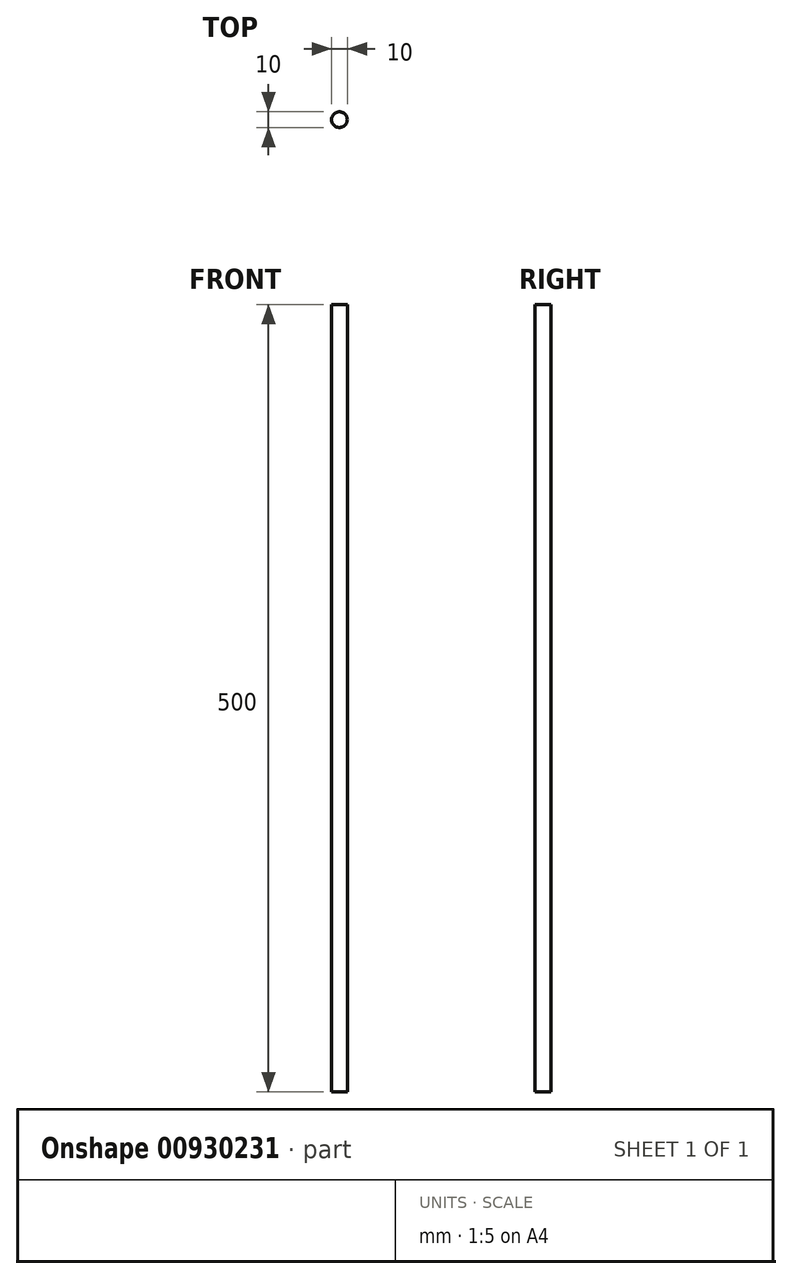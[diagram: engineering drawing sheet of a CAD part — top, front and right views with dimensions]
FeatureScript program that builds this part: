
annotation { "Feature Type Name" : "Feature", "Feature Type Description" : "" }
export const myFeature = defineFeature(function(context is Context, id is Id, definition is map)
    precondition{}
    {
        {
            var Q0;
            Q0=qCreatedBy(makeId("Top.planeOp"),FACE);
            var sketch = newSketch(context, id + "F0", { "sketchPlane" : qUnion([Q0])});
            skCircle(sketch, "E0", {"center": v(0, 0) * mm, "radius": 5 * mm});
            skSolve(sketch);
        }
        {
            var Q0;
            Q0=qSketchRegion(id+"F0",true);
            extrude(context, id + "F1", {"entities" : qUnion([Q0]), "depth" : 500 * mm, "offsetDistance" : 25 * mm});
        }
    });
